# Revit family: E-61-AQ_RFA
name_source: partatom
category: Aparatos sanitarios
units: mm (PartAtom-declared; Revit-internal decimal feet)

## family parameters
Compartido = No
Corte con vacíos al cargar = No
Cota de conector redondo = Diámetro de uso
Número OmniClass = 23.45.00.00
Punto de cálculo de habitación = No
Se basa en plano de trabajo = No
Siempre vertical = Sí
Tipo de pieza = Normal
Título OmniClass = Sanitary, Laundry, and Cleaning Equipment

## types (1)
- E-61-AQ
    Comentarios de tipo = Shower Faucet
    Data Sheet = https://helvex.com.mx
    Descripción = Embeddable Weldable Assembly
    Elevación por defecto = 0"
    Fabricante = HELVEX
    Features = Threaded Body To Weld; Left Val-Vex I Or Left And Right Val-Vex V ¼" Turn To Ceramic Disc
    Inlet Threads = ½" - 14 NPT
    Instructive = https://helvex.com.mx
    Max. Working Pressure = 85.3 psi
    Min. Working Pressure = 2.8 psi
    Modelo = E-61-AQ
    Support Base Diameter = 1"
    Total Height = 3"
    Total Length = 4"
    URL = https://helvex.com.mx

## geometry (parser evidence)
native form markers: Sweep x3
no freeform markers — native parametric forms only
